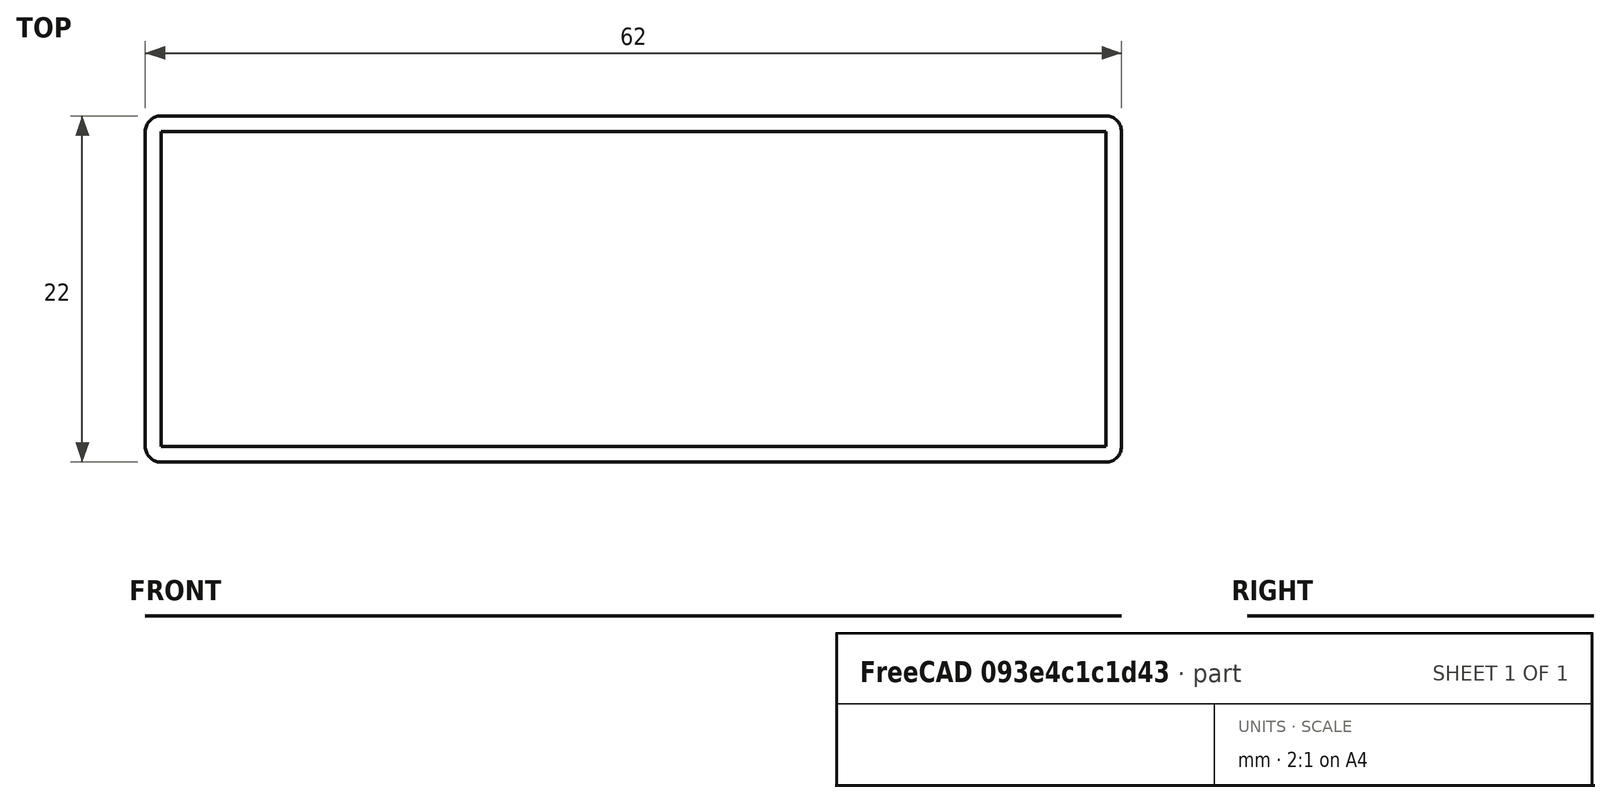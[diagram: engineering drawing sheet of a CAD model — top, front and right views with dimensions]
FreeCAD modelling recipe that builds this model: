
FCSTD DOCUMENT  (FreeCAD 0.20R27319 (Git))
Label: BDM-case
License: All rights reserved
LicenseURL: http://en.wikipedia.org/wiki/All_rights_reserved
objects: Sketcher::SketchObject×2, PartDesign::Body×1, Part::Offset2D×1
note: 4 computed .brp shape members not serialized (recipe doc carries the construction recipe); baked Part::Feature solids carry a one-line shape summary decoded from their .brp

FEATURE [Sketcher::SketchObject] Sketch
  FullyConstrained = true
  MapMode = 5
  Support = -> [XY_Plane]
  sketch-geometry (5):
    g0: LineSegment StartX=-30 StartY=10 StartZ=0 EndX=-30 EndY=-10 EndZ=0
    g1: LineSegment StartX=-30 StartY=-10 StartZ=0 EndX=30 EndY=-10 EndZ=0
    g2: LineSegment StartX=30 StartY=-10 StartZ=0 EndX=30 EndY=10 EndZ=0
    g3: LineSegment StartX=30 StartY=10 StartZ=0 EndX=-30 EndY=10 EndZ=0
    g4: GeomPoint X=0 Y=0 Z=0
  constraints (12):
    c: Coincident(g0,g1)
    c: Coincident(g1,g2)
    c: Coincident(g2,g3)
    c: Coincident(g3,g0)
    c: Horizontal(g1)
    c: Horizontal(g3)
    c: Vertical(g0)
    c: Vertical(g2)
    c: Symmetric(g1,g0,g4)
    c: Coincident(g4,g-1)
    c: Distance(g3) = 60
    c: Distance(g2) = 20
FEATURE [Sketcher::SketchObject] Sketch002
  ExternalGeometry = -> [Sketch]
  FullyConstrained = true
  MapMode = 5
  Support = -> [XY_Plane]
  sketch-geometry (16):
    g0: LineSegment StartX=-30 StartY=10 StartZ=0 EndX=-29 EndY=10 EndZ=0
    g1: LineSegment StartX=-29 StartY=10 StartZ=0 EndX=-29 EndY=9 EndZ=0
    g2: LineSegment StartX=-29 StartY=9 StartZ=0 EndX=-30 EndY=9 EndZ=0
    g3: LineSegment StartX=-30 StartY=9 StartZ=0 EndX=-30 EndY=10 EndZ=0
    g4: LineSegment StartX=-30 StartY=-10 StartZ=0 EndX=-29 EndY=-10 EndZ=0
    g5: LineSegment StartX=-29 StartY=-10 StartZ=0 EndX=-29 EndY=-9 EndZ=0
    g6: LineSegment StartX=-29 StartY=-9 StartZ=0 EndX=-30 EndY=-9 EndZ=0
    g7: LineSegment StartX=-30 StartY=-9 StartZ=0 EndX=-30 EndY=-10 EndZ=0
    g8: LineSegment StartX=30 StartY=-10 StartZ=0 EndX=29 EndY=-10 EndZ=0
    g9: LineSegment StartX=29 StartY=-10 StartZ=0 EndX=29 EndY=-9 EndZ=0
    g10: LineSegment StartX=29 StartY=-9 StartZ=0 EndX=30 EndY=-9 EndZ=0
    g11: LineSegment StartX=30 StartY=-9 StartZ=0 EndX=30 EndY=-10 EndZ=0
    g12: LineSegment StartX=30 StartY=10 StartZ=0 EndX=29 EndY=10 EndZ=0
    g13: LineSegment StartX=29 StartY=10 StartZ=0 EndX=29 EndY=9 EndZ=0
    g14: LineSegment StartX=29 StartY=9 StartZ=0 EndX=30 EndY=9 EndZ=0
    g15: LineSegment StartX=30 StartY=9 StartZ=0 EndX=30 EndY=10 EndZ=0
  constraints (44):
    c: Coincident(g0,g1)
    c: Coincident(g1,g2)
    c: Coincident(g2,g3)
    c: Coincident(g3,g0)
    c: Horizontal(g0)
    c: Horizontal(g2)
    c: Vertical(g1)
    c: Vertical(g3)
    c: Coincident(g4,g5)
    c: Coincident(g5,g6)
    c: Coincident(g6,g7)
    c: Coincident(g7,g4)
    c: Horizontal(g4)
    c: Horizontal(g6)
    c: Vertical(g5)
    c: Vertical(g7)
    c: Coincident(g8,g9)
    c: Coincident(g9,g10)
    c: Coincident(g10,g11)
    c: Coincident(g11,g8)
    c: Horizontal(g8)
    c: Horizontal(g10)
    c: Vertical(g9)
    c: Vertical(g11)
    c: Coincident(g12,g13)
    c: Coincident(g13,g14)
    c: Coincident(g14,g15)
    c: Coincident(g15,g12)
    c: Horizontal(g12)
    c: Horizontal(g14)
    c: Vertical(g13)
    c: Vertical(g15)
    c: Equal(g12,g15)
    c: Equal(g15,g11)
    c: Equal(g11,g8)
    c: Equal(g8,g0)
    c: Equal(g0,g3)
    c: Equal(g3,g7)
    c: Equal(g7,g4)
    c: Distance(g0) = 1
    c: Coincident(g12,g-6)
    c: Coincident(g8,g-5)
    c: Coincident(g4,g-4)
    c: Coincident(g0,g-3)
FEATURE [PartDesign::Body] Body
  Group = -> [Sketch,Sketch002]
  Origin = -> Origin
FEATURE [Part::Offset2D] Offset2D
  Fill = true
  Intersection = false
  Join = 0
  Mode = 1
  SelfIntersection = false
  Source = -> Sketch
  Value = 1
